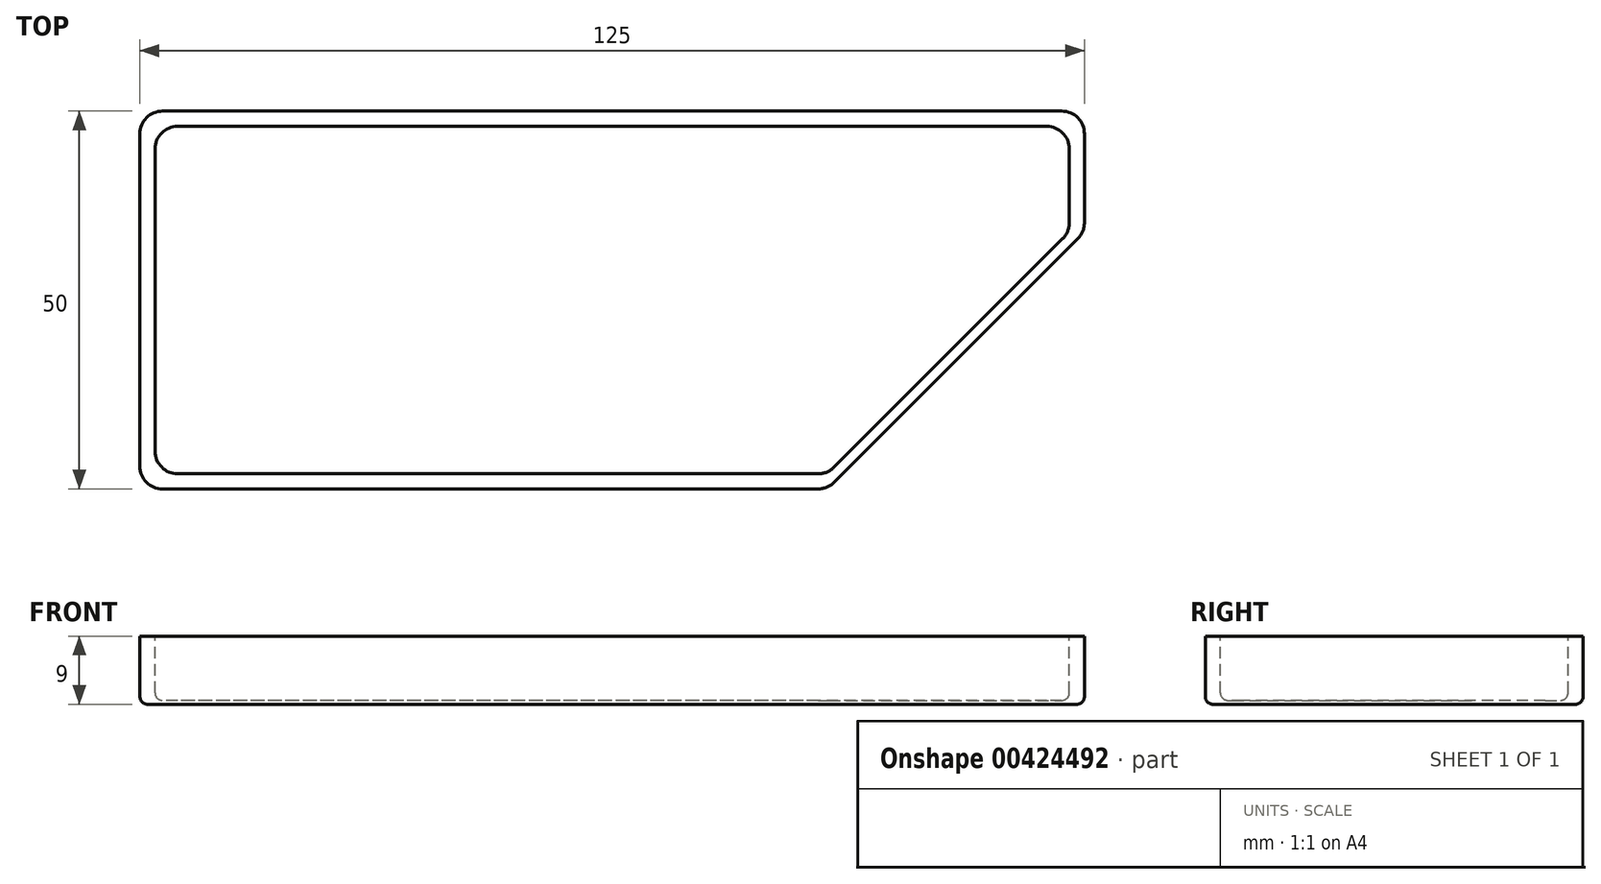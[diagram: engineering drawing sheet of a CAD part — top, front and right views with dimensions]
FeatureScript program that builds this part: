
annotation { "Feature Type Name" : "Feature", "Feature Type Description" : "" }
export const myFeature = defineFeature(function(context is Context, id is Id, definition is map)
    precondition{}
    {
        {
            var Q0;
            Q0=qCreatedBy(makeId("Top.planeOp"),FACE);
            var sketch = newSketch(context, id + "F0", { "sketchPlane" : qUnion([Q0])});
            skLineSegment(sketch, "E0.top", {"start": v(28.5, -25) * mm, "end": v(-62.5, -25) * mm});
            skLineSegment(sketch, "E0.right", {"start": v(-62.5, 25) * mm, "end": v(-62.5, -25) * mm});
            skPoint(sketch, "E0.middle", {"position": v(0, 0) * mm});
            skPoint(sketch, "E1.orphan", {"position": v(62.5, 25) * mm});
            skLineSegment(sketch, "E2", {"start": v(-62.5, 25) * mm, "end": v(62.5, 25) * mm});
            skLineSegment(sketch, "E3", {"start": v(62.5, 9) * mm, "end": v(62.5, 25) * mm});
            skLineSegment(sketch, "E4", {"start": v(62.5, 9) * mm, "end": v(28.5, -25) * mm});
            skPoint(sketch, "E5.orphan", {"position": v(62.5, -25) * mm});
            skSolve(sketch);
        }
        {
            var Q0;
            Q0=makeQuery(id+"F0.imprint","IMPRINT",FACE,{"disambiguationData":[TD([[makeQuery(id+"F0.imprint","IMPRINT",EDGE,{"derivedFrom":sQuery(id+"F0.wireOp",EDGE,"E0.bottom")}),1.0]])]});
            var Q1;
            Q1=makeQuery(id+"F0.imprint","IMPRINT",FACE,{"disambiguationData":[TD([[makeQuery(id+"F0.imprint","IMPRINT",EDGE,{"derivedFrom":sQuery(id+"F0.wireOp",EDGE,"E0.top")}),-1.0]])]});
            extrude(context, id + "F1", {"entities" : qUnion([Q0, Q1]), "depth" : 9 * mm});
        }
        {
            var Q0;
            Q0=makeQuery(id+"F1.opExtrude","CAP_FACE",FACE,{"disambiguationData":[OSD([sQuery(id+"F0.wireOp",EDGE,"E0.bottom"),sQuery(id+"F0.wireOp",EDGE,"E0.top"),sQuery(id+"F0.wireOp",EDGE,"E0.left"),sQuery(id+"F0.wireOp",EDGE,"E0.right"),sQuery(id+"F0.wireOp",EDGE,"9dEclZIP-fIdI-Qplm-MATt-ZQUbisnn2c5j")])],"isStart":false});
            var sketch = newSketch(context, id + "F2", { "sketchPlane" : qUnion([Q0])});
            skLineSegment(sketch, "E6.bottom", {"start": v(60.5, 23) * mm, "end": v(-60.5, 23) * mm});
            skLineSegment(sketch, "E6.top", {"start": v(28.5, -23) * mm, "end": v(-60.5, -23) * mm});
            skLineSegment(sketch, "E6.left", {"start": v(60.5, 23) * mm, "end": v(60.5, 9) * mm});
            skLineSegment(sketch, "E6.right", {"start": v(-60.5, 23) * mm, "end": v(-60.5, -23) * mm});
            skPoint(sketch, "E6.middle", {"position": v(0, 0) * mm});
            skLineSegment(sketch, "E7", {"start": v(28.5, -23) * mm, "end": v(60.5, 9) * mm});
            skPoint(sketch, "E8.orphan", {"position": v(60.5, -23) * mm});
            skSolve(sketch);
        }
        {
            var Q0;
            {var subQ1=sQuery(id+"F2.wireOp",EDGE,"E6.top");Q0=makeQuery(id+"F2.imprint","IMPRINT",FACE,{"disambiguationData":[TD([[makeQuery(id+"F2.imprint","IMPRINT",EDGE,{"derivedFrom":subQ1}),-1.0]])]});}
            extrude(context, id + "F3", {"entities" : qUnion([Q0]), "operationType" : NewBodyOperationType.REMOVE, "oppositeDirection" : true, "depth" : 8.5 * mm});
        }
        {
            var Q0;
            Q0=makeQuery(id+"F3.boolean.opBoolean","COPY",EDGE,{"derivedFrom":makeQuery(id+"F3.opExtrude","SWEPT_EDGE",EDGE,{"disambiguationData":[OSD([sQuery(id+"F2.wireOp",EDGE,"E6.bottom"),sQuery(id+"F2.wireOp",EDGE,"E6.right")])]})});
            var Q1;
            Q1=makeQuery(id+"F3.boolean.opBoolean","COPY",EDGE,{"derivedFrom":makeQuery(id+"F3.opExtrude","SWEPT_EDGE",EDGE,{"disambiguationData":[OSD([sQuery(id+"F2.wireOp",EDGE,"E6.bottom"),sQuery(id+"F2.wireOp",EDGE,"E6.left")])]})});
            var Q2;
            Q2=makeQuery(id+"F3.boolean.opBoolean","COPY",EDGE,{"derivedFrom":makeQuery(id+"F3.opExtrude","SWEPT_EDGE",EDGE,{"disambiguationData":[OSD([sQuery(id+"F2.wireOp",EDGE,"E6.left"),sQuery(id+"F2.wireOp",EDGE,"E7")])]})});
            var Q3;
            Q3=makeQuery(id+"F3.boolean.opBoolean","COPY",EDGE,{"derivedFrom":makeQuery(id+"F3.opExtrude","SWEPT_EDGE",EDGE,{"disambiguationData":[OSD([sQuery(id+"F2.wireOp",EDGE,"E6.top"),sQuery(id+"F2.wireOp",EDGE,"E7")])]})});
            var Q4;
            Q4=makeQuery(id+"F3.boolean.opBoolean","COPY",EDGE,{"derivedFrom":makeQuery(id+"F3.opExtrude","SWEPT_EDGE",EDGE,{"disambiguationData":[OSD([sQuery(id+"F2.wireOp",EDGE,"E6.top"),sQuery(id+"F2.wireOp",EDGE,"E6.right")])]})});
            var Q5;
            Q5=makeQuery(id+"F1.opExtrude","SWEPT_EDGE",EDGE,{"disambiguationData":[OSD([sQuery(id+"F0.wireOp",EDGE,"E2"),sQuery(id+"F0.wireOp",EDGE,"E3")])]});
            var Q6;
            Q6=makeQuery(id+"F1.opExtrude","SWEPT_EDGE",EDGE,{"disambiguationData":[OSD([sQuery(id+"F0.wireOp",EDGE,"E3"),sQuery(id+"F0.wireOp",EDGE,"E4")])]});
            var Q7;
            Q7=makeQuery(id+"F1.opExtrude","SWEPT_EDGE",EDGE,{"disambiguationData":[OSD([sQuery(id+"F0.wireOp",EDGE,"E0.top"),sQuery(id+"F0.wireOp",EDGE,"E4")])]});
            var Q8;
            Q8=makeQuery(id+"F1.opExtrude","SWEPT_EDGE",EDGE,{"disambiguationData":[OSD([sQuery(id+"F0.wireOp",EDGE,"E0.right"),sQuery(id+"F0.wireOp",EDGE,"E2")])]});
            var Q9;
            Q9=makeQuery(id+"F1.opExtrude","SWEPT_EDGE",EDGE,{"disambiguationData":[OSD([sQuery(id+"F0.wireOp",EDGE,"E0.top"),sQuery(id+"F0.wireOp",EDGE,"E0.right")])]});
            fillet(context, id + "F4", {"entities" : qUnion([Q0, Q1, Q2, Q3, Q4, Q5, Q6, Q7, Q8, Q9]), "radius" : 3 * mm, "tangentPropagation" : true, "allowEdgeOverflow" : false});
        }
        {
            var Q0;
            Q0=makeQuery(id+"F3.boolean.opBoolean","COPY",FACE,{"derivedFrom":makeQuery(id+"F3.opExtrude","CAP_FACE",FACE,{"disambiguationData":[OSD([sQuery(id+"F2.wireOp",EDGE,"E6.bottom"),sQuery(id+"F2.wireOp",EDGE,"E6.top"),sQuery(id+"F2.wireOp",EDGE,"E6.left"),sQuery(id+"F2.wireOp",EDGE,"E6.right"),sQuery(id+"F2.wireOp",EDGE,"E7")])],"isStart":false})});
            var Q1;
            Q1=makeQuery(id+"F1.opExtrude","CAP_FACE",FACE,{"disambiguationData":[OSD([sQuery(id+"F0.wireOp",EDGE,"E0.top"),sQuery(id+"F0.wireOp",EDGE,"E0.right"),sQuery(id+"F0.wireOp",EDGE,"E2"),sQuery(id+"F0.wireOp",EDGE,"E3"),sQuery(id+"F0.wireOp",EDGE,"E4")])],"isStart":true});
            fillet(context, id + "F5", {"entities" : qUnion([Q0, Q1]), "radius" : 1 * mm, "tangentPropagation" : true, "allowEdgeOverflow" : false});
        }
    });
